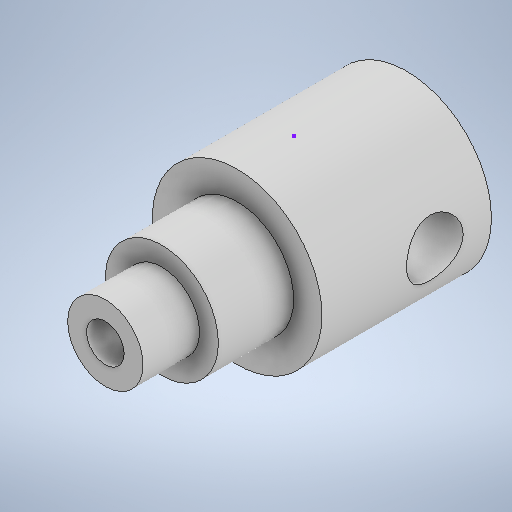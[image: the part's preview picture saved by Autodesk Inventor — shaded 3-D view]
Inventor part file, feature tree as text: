
AUTODESK INVENTOR PART (.ipt)
format: ipt  version: 2025.2 (Build 292293000, 293)  size: 299,520 bytes
history: native  units: in
note: dims shown in document units (in); Inventor stores cm internally (conversion verified against a paired STEP export)
features: sketch x8, extrude x5, plane x2
ambient origin geometry x8: Origin, YZ Plane, XZ Plane, XY Plane, X Axis, Y Axis, Z Axis, Center Point
bodies: Solid1 (feature_tree)
feature tree (15):
  extrude  "Extrusion1"  Depth=1.1811in TaperAngle=0.0deg
  extrude  "Extrusion2"  Depth=1.5748in TaperAngle=0.0deg
  extrude  "Extrusion3"  Depth=1.1811in TaperAngle=0.0deg
  extrude  "Extrusion4"  Depth=0.7874in TaperAngle=0.0deg
  plane  "Work Plane1"
  sketch  "Sketch5"  dims[d12=-1.7717in d20=2.3622in d21=0.0in]
  sketch  "Sketch6"  dims[d22=-1.7717in]
  plane  "Work Plane2"
  extrude  "Extrusion5"  Depth=2.3622in TaperAngle=0.0deg
  sketch  "Sketch8"  dims[d26=0.0in d27=0.0in]
  sketch  "Sketch1"  dims[d0=3.5433in d1=1.1811in d2=0.0in]
  sketch  "Sketch2"  dims[d3=2.3622in d4=1.5748in d5=0.0in]
  sketch  "Sketch3"  dims[d6=1.5748in d7=1.1811in d8=0.0in]
  sketch  "Sketch4"  dims[d9=0.7874in d10=1.1811in d11=0.0in]
  sketch  "Sketch7"  dims[d25=1.1811in]
